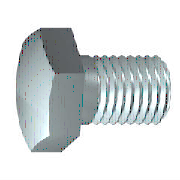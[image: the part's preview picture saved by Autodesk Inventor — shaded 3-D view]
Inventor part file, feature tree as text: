
AUTODESK INVENTOR PART (.ipt)
format: ipt  version: 2023.1 (Build 271208000, 208)  size: 208,896 bytes
history: native  units: mm (DEFAULTED — no unit token found)
features: sketch x4, other x3, revolve x2, extrude x2, fillet x1
ambient origin geometry x8: Origin, YZ Plane, XZ Plane, XY Plane, X Axis, Y Axis, Z Axis, Center Point
bodies: Solid1 (feature_tree)
feature tree (12):
  revolve  "Revolution1"  Angle=45.0deg
  extrude  "Extrusion1"  TaperAngle=60.0deg  [1 undecoded]
  revolve  "Revolution2"  Angle=30.0deg
  extrude  "Extrusion2"  TaperAngle=0.0deg  [1 undecoded]
  other  "MSC_A1"
  other  "MSC_PF1"
  other  "MSC_PT1"
  fillet  "Fillet1"  [1 undecoded]
  sketch  "Sketch2"  dims[d3=30.0deg d5=45.0deg]
  sketch  "Sketch3"  dims[d8=90.0deg d9=60.0deg]
  sketch  "Sketch4"  dims[d13=0.0mm d14=30.0deg]
  sketch  "Sketch5"  dims[d16=90.0deg d18=0.0mm d22=0.0mm d23=0.0mm d25=0.0mm d26=0.0mm d27=18.0mm d28=2.0mm d29=0.0mm d30=0.6mm d31=0.0mm]
note: 3 required parameter values undecoded (feature->parameter linkage not recoverable at this tier; creation-order binding heuristic only, values carry confidence <= 0.55)
